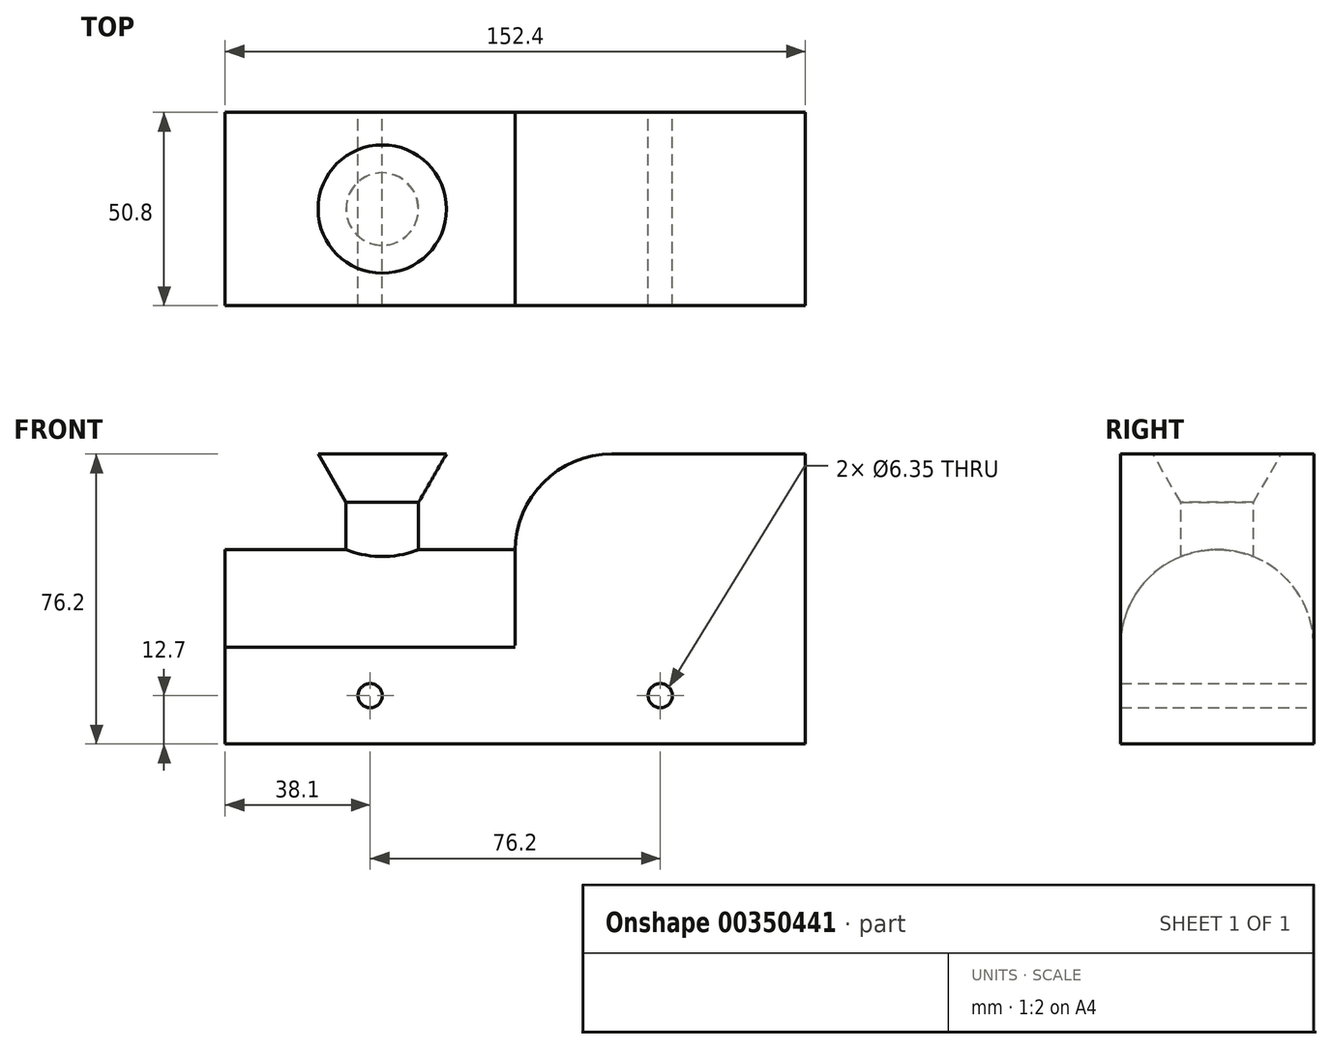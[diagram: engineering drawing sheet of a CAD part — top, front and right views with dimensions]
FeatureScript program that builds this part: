
annotation { "Feature Type Name" : "Feature", "Feature Type Description" : "" }
export const myFeature = defineFeature(function(context is Context, id is Id, definition is map)
    precondition{}
    {
        {
            var Q0;
            Q0=qCreatedBy(makeId("Front.planeOp"),FACE);
            var sketch = newSketch(context, id + "F0", { "sketchPlane" : qUnion([Q0])});
            skLineSegment(sketch, "E0.bottom", {"start": v(-76.2, 38.1) * mm, "end": v(76.2, 38.1) * mm});
            skLineSegment(sketch, "E0.top", {"start": v(-76.2, -38.1) * mm, "end": v(76.2, -38.1) * mm});
            skLineSegment(sketch, "E0.left", {"start": v(-76.2, 38.1) * mm, "end": v(-76.2, -38.1) * mm});
            skLineSegment(sketch, "E0.right", {"start": v(76.2, 38.1) * mm, "end": v(76.2, -38.1) * mm});
            skPoint(sketch, "E0.middle", {"position": v(0, 0) * mm});
            skLineSegment(sketch, "E1", {"start": v(0, 12.7) * mm, "end": v(0, 0) * mm});
            skLineSegment(sketch, "E2", {"start": v(25.4, 38.1) * mm, "end": v(76.2, 38.1) * mm});
            skArc(sketch, "E3.filletArc", {"start": v(25.4, 38.1) * mm, "mid": v(7.44, 30.66) * mm, "end": v(0, 12.7) * mm});
            skCircle(sketch, "E4", {"center": v(-38.1, -25.4) * mm, "radius": 3.18 * mm});
            skCircle(sketch, "E5", {"center": v(38.1, -25.4) * mm, "radius": 3.18 * mm});
            skLineSegment(sketch, "E6.bottom", {"start": v(-25.4, -12.7) * mm, "end": v(-44.45, -12.7) * mm});
            skLineSegment(sketch, "E6.top", {"start": v(-25.4, 25.4) * mm, "end": v(-44.45, 25.4) * mm});
            skLineSegment(sketch, "E6.left", {"start": v(-25.4, -12.7) * mm, "end": v(-25.4, 25.4) * mm});
            skLineSegment(sketch, "E6.right", {"start": v(-44.45, -12.7) * mm, "end": v(-44.45, 25.4) * mm});
            skLineSegment(sketch, "E7", {"start": v(-25.4, 25.4) * mm, "end": v(-18.07, 38.1) * mm});
            skLineSegment(sketch, "E8", {"start": v(-18.07, 38.1) * mm, "end": v(-51.78, 38.22) * mm});
            skLineSegment(sketch, "E9", {"start": v(-51.78, 38.1) * mm, "end": v(-44.45, 25.4) * mm});
            skLineSegment(sketch, "E10", {"start": v(-34.93, 38.16) * mm, "end": v(-34.92, -12.7) * mm});
            skLineSegment(sketch, "E11", {"start": v(-76.2, -12.7) * mm, "end": v(0, -12.7) * mm});
            skLineSegment(sketch, "E12", {"start": v(0, -12.7) * mm, "end": v(0, 0) * mm});
            skSolve(sketch);
        }
        {
            var Q0;
            Q0=makeQuery(id+"F0.imprint","IMPRINT",FACE,{"disambiguationData":[TD([[makeQuery(id+"F0.imprint","IMPRINT",EDGE,{"derivedFrom":sQuery(id+"F0.wireOp",EDGE,"E0.top")}),1.0]])]});
            extrude(context, id + "F1", {"entities" : qUnion([Q0]), "endBound" : BoundingType.SYMMETRIC, "depth" : 50.8 * mm, "hasSecondDirection" : true, "secondDirectionOppositeDirection" : true, "secondDirectionDepth" : 25.4 * mm});
        }
        {
            var Q0;
            {var subQ0=sQuery(id+"F0.wireOp",EDGE,"E9");Q0=makeQuery(id+"F0.imprint","IMPRINT",FACE,{"disambiguationData":[TD([[makeQuery(id+"F0.imprint","IMPRINT",EDGE,{"derivedFrom":subQ0}),1.0]])]});}
            var Q1;
            {var subQ0=sQuery(id+"F0.wireOp",EDGE,"E6.right");Q1=makeQuery(id+"F0.imprint","IMPRINT",FACE,{"disambiguationData":[TD([[makeQuery(id+"F0.imprint","IMPRINT",EDGE,{"derivedFrom":subQ0}),-1.0]])]});}
            var Q2;
            Q2=sQuery(id+"F0.wireOp",EDGE,"E10");
            revolve(context, id + "F2", {"operationType" : NewBodyOperationType.ADD, "entities" : qUnion([Q0, Q1]), "axis" : qUnion([Q2]), "revolveType" : RevolveType.FULL});
        }
        {
            var Q0;
            Q0=makeQuery(id+"F1.opExtrude","SWEPT_FACE",FACE,{"disambiguationData":[OSD([sQuery(id+"F0.wireOp",EDGE,"E0.left")])]});
            var sketch = newSketch(context, id + "F3", { "sketchPlane" : qUnion([Q0])});
            skCircle(sketch, "E13", {"center": v(0, -12.4) * mm, "radius": 25.4 * mm});
            skPoint(sketch, "E13.first.point", {"position": v(0, 13) * mm});
            skPoint(sketch, "E13.second.point", {"position": v(-25.4, -12.7) * mm});
            skPoint(sketch, "E13.third.point", {"position": v(25.4, -12.7) * mm});
            skSolve(sketch);
        }
        {
            var Q0;
            {var subQ1=sQuery(id+"F0.wireOp",EDGE,"E0.left");var subQ2=makeQuery(id+"F1.opExtrude","SWEPT_EDGE",EDGE,{"disambiguationData":[OSD([subQ1,sQuery(id+"F0.wireOp",EDGE,"E11")])]});Q0=makeQuery(id+"F3.imprint","IMPRINT",FACE,{"disambiguationData":[TD([[makeQuery(id+"F3.imprint","IMPRINT",EDGE,{"derivedFrom":subQ2}),-1.0]])]});}
            extrude(context, id + "F4", {"entities" : qUnion([Q0]), "operationType" : NewBodyOperationType.ADD, "oppositeDirection" : true, "depth" : 76.2 * mm});
        }
    });
